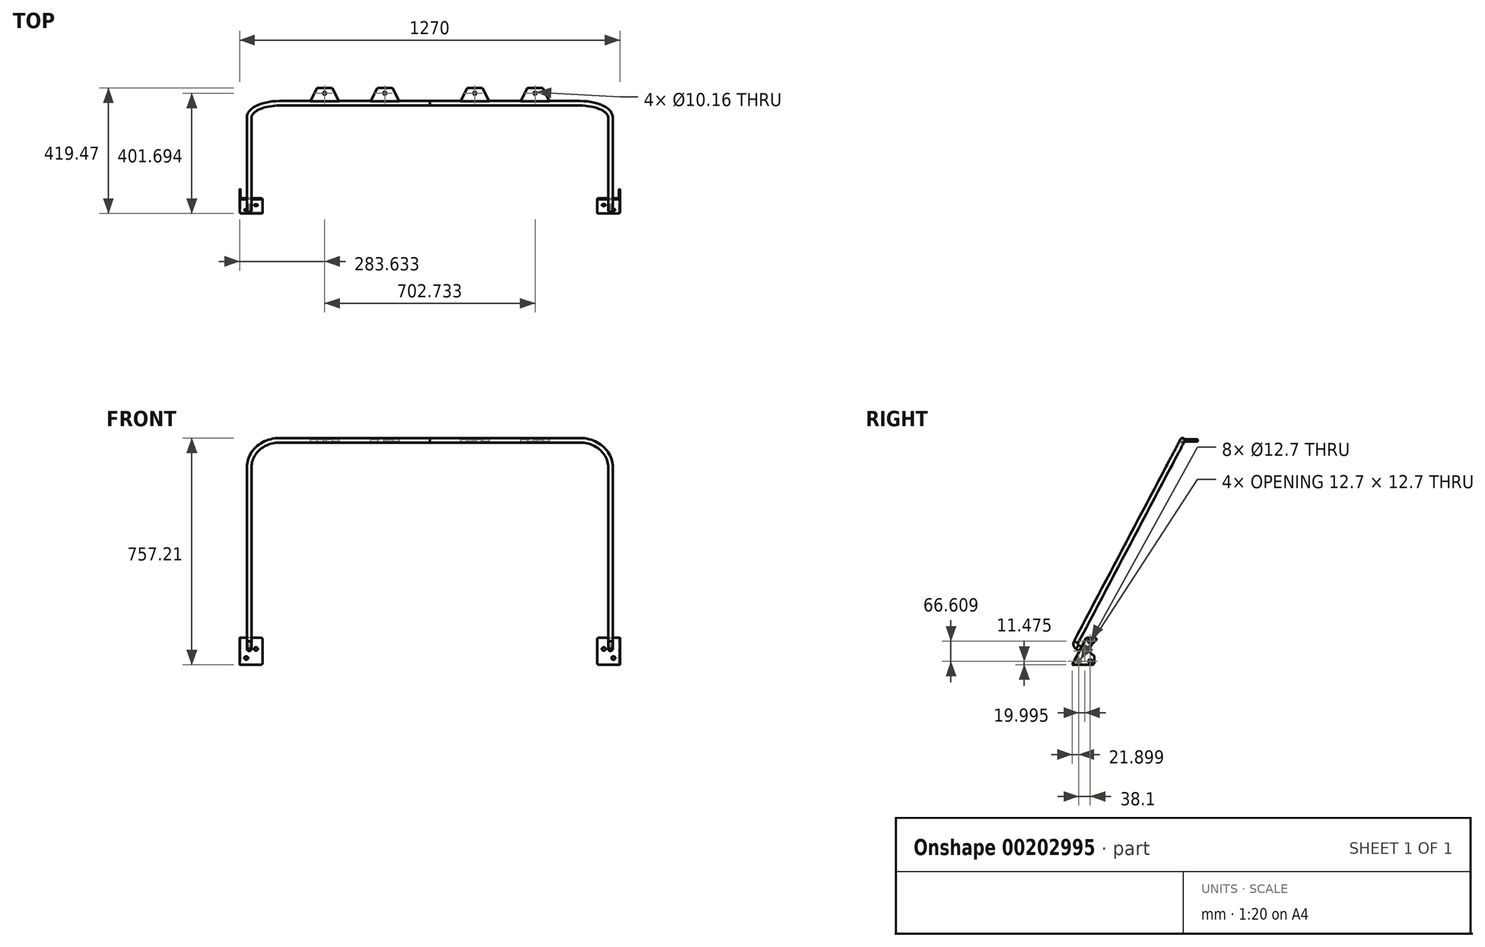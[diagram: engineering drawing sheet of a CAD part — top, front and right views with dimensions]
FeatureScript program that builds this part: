
annotation { "Feature Type Name" : "Feature", "Feature Type Description" : "" }
export const myFeature = defineFeature(function(context is Context, id is Id, definition is map)
    precondition{}
    {
        {
            var Q0;
            Q0=qCreatedBy(makeId("Right.planeOp"),FACE);
            var sketch = newSketch(context, id + "F0", { "sketchPlane" : qUnion([Q0])});
            skLineSegment(sketch, "E0", {"start": v(0, 0) * mm, "end": v(-47.4, -89.86) * mm});
            skLineSegment(sketch, "E1", {"start": v(-47.4, -89.86) * mm, "end": v(-50.58, -89.86) * mm});
            skLineSegment(sketch, "E2", {"start": v(-50.58, -89.86) * mm, "end": v(-3.17, 0) * mm});
            skLineSegment(sketch, "E3", {"start": v(-3.17, 0) * mm, "end": v(0, 0) * mm});
            skSolve(sketch);
        }
        {
            var Q0;
            Q0 = qSketchRegion(id + "F0", true);
            extrude(context, id + "F1", {"entities" : qUnion([Q0]), "depth" : 76.2 * mm});
        }
        {
            var Q0;
            Q0=qCreatedBy(makeId("Right.planeOp"),FACE);
            var sketch = newSketch(context, id + "F2", { "sketchPlane" : qUnion([Q0])});
            skLineSegment(sketch, "E4", {"start": v(-3.18, 0) * mm, "end": v(-50.58, -89.86) * mm});
            skLineSegment(sketch, "E5", {"start": v(-50.58, -89.86) * mm, "end": v(22.53, -89.86) * mm});
            skLineSegment(sketch, "E6", {"start": v(22.53, -89.86) * mm, "end": v(22.53, -58.72) * mm});
            skLineSegment(sketch, "E7", {"start": v(-3.17, 0) * mm, "end": v(40.86, 0) * mm});
            skFitSpline(sketch, "E8", {"points": [v(40.86, 0) * mm, v(22.53, -58.72) * mm], "startDerivative": vector(-122.58, -77.31) * mm, "endDerivative": vector(65.99, -20.96) * mm});
            skSolve(sketch);
        }
        {
            var Q0;
            Q0 = qSketchRegion(id + "F2", true);
            extrude(context, id + "F3", {"entities" : qUnion([Q0]), "operationType" : NewBodyOperationType.ADD, "depth" : 3.17 * mm});
        }
        {
            var Q0;
            Q0=makeQuery(id+"F1.opExtrude","SWEPT_FACE",FACE,{"disambiguationData":[OSD([sQuery(id+"F0.wireOp",EDGE,"E2")])]});
            var sketch = newSketch(context, id + "F4", { "sketchPlane" : qUnion([Q0])});
            skCircle(sketch, "E9", {"center": v(54.23, -43.4) * mm, "radius": 6.35 * mm});
            skCircle(sketch, "E10", {"center": v(21.97, -77.68) * mm, "radius": 6.35 * mm});
            skSolve(sketch);
        }
        {
            var Q0;
            Q0 = qSketchRegion(id + "F4", true);
            var Q1;
            Q1=makeQuery(id+"F1.opExtrude","SWEPT_FACE",FACE,{"disambiguationData":[OSD([sQuery(id+"F0.wireOp",EDGE,"E0")])]});
            extrude(context, id + "F5", {"entities" : qUnion([Q0]), "operationType" : NewBodyOperationType.REMOVE, "endBound" : BoundingType.UP_TO_SURFACE, "oppositeDirection" : true, "endBoundEntityFace" : qUnion([Q1]), "depth" : 25.4 * mm});
        }
        {
            var Q0;
            Q0=makeQuery(id+"F3.boolean.opBoolean","MERGE",FACE,{"derivedFrom":[makeQuery(id+"F1.opExtrude","CAP_FACE",FACE,{"disambiguationData":[OSD([sQuery(id+"F0.wireOp",EDGE,"E0"),sQuery(id+"F0.wireOp",EDGE,"E1"),sQuery(id+"F0.wireOp",EDGE,"E2"),sQuery(id+"F0.wireOp",EDGE,"E3")])],"isStart":true}),makeQuery(id+"F3.opExtrude","CAP_FACE",FACE,{"disambiguationData":[OSD([sQuery(id+"F2.wireOp",EDGE,"E4"),sQuery(id+"F2.wireOp",EDGE,"E5"),sQuery(id+"F2.wireOp",EDGE,"E6"),sQuery(id+"F2.wireOp",EDGE,"E7"),sQuery(id+"F2.wireOp",EDGE,"E8")])],"isStart":true})]});
            var sketch = newSketch(context, id + "F6", { "sketchPlane" : qUnion([Q0])});
            skCircle(sketch, "E11", {"center": v(-8.56, -11.78) * mm, "radius": 6.35 * mm});
            skCircle(sketch, "E12", {"center": v(8.69, -44.87) * mm, "radius": 6.35 * mm});
            skCircle(sketch, "E13", {"center": v(-9.42, -78.39) * mm, "radius": 6.35 * mm});
            skCircle(sketch, "E14", {"center": v(28.68, -78.39) * mm, "radius": 6.35 * mm});
            skSolve(sketch);
        }
        {
            var Q0;
            Q0 = qSketchRegion(id + "F6", true);
            var Q1;
            Q1=makeQuery(id+"F3.opExtrude","CAP_FACE",FACE,{"disambiguationData":[OSD([sQuery(id+"F2.wireOp",EDGE,"E4"),sQuery(id+"F2.wireOp",EDGE,"E5"),sQuery(id+"F2.wireOp",EDGE,"E6"),sQuery(id+"F2.wireOp",EDGE,"E7"),sQuery(id+"F2.wireOp",EDGE,"E8")])],"isStart":false});
            extrude(context, id + "F7", {"entities" : qUnion([Q0]), "operationType" : NewBodyOperationType.REMOVE, "endBound" : BoundingType.UP_TO_SURFACE, "oppositeDirection" : true, "endBoundEntityFace" : qUnion([Q1]), "depth" : 25.4 * mm});
        }
        {
            var Q0;
            Q0=qCreatedBy(makeId("Right.planeOp"),FACE);
            cPlane(context, id + "F8", {"entities" : qUnion([Q0]), "cplaneType" : CPlaneType.OFFSET, "offset" : 635 * mm, "width" : 152.4 * mm, "height" : 152.4 * mm});
        }
        {
            var Q0;
            Q0=qCreatedBy(makeId("Right.planeOp"),FACE);
            cPlane(context, id + "F9", {"entities" : qUnion([Q0]), "cplaneType" : CPlaneType.OFFSET, "offset" : 31.75 * mm, "width" : 152.4 * mm, "height" : 152.4 * mm});
        }
        {
            var Q0;
            Q0=qCreatedBy(id+"F9.planeOp",FACE);
            var sketch = newSketch(context, id + "F10", { "sketchPlane" : qUnion([Q0])});
            skLineSegment(sketch, "E15", {"start": v(-22.79, -37.18) * mm, "end": v(-33.75, -30.77) * mm});
            skArc(sketch, "E16", {"start": v(-33.75, -30.77) * mm, "mid": v(-39.05, -23.33) * mm, "end": v(-37.97, -14.25) * mm});
            skLineSegment(sketch, "E17", {"start": v(-37.97, -14.25) * mm, "end": v(270.14, 569.86) * mm});
            skLineSegment(sketch, "E18", {"start": v(-37.97, -14.25) * mm, "end": v(-16.63, -25.51) * mm});
            skSolve(sketch);
        }
        {
            var Q0;
            Q0=makeQuery(id+"F1.opExtrude","SWEPT_FACE",FACE,{"disambiguationData":[OSD([sQuery(id+"F0.wireOp",EDGE,"E2")])]});
            cPlane(context, id + "F11", {"entities" : qUnion([Q0]), "cplaneType" : CPlaneType.OFFSET, "offset" : 24.13 * mm, "width" : 152.4 * mm, "height" : 152.4 * mm});
        }
        {
            var Q0;
            Q0=qCreatedBy(id+"F11.planeOp",FACE);
            var sketch = newSketch(context, id + "F12", { "sketchPlane" : qUnion([Q0])});
            skLineSegment(sketch, "E19", {"start": v(133.35, 731.68) * mm, "end": v(635, 731.68) * mm});
            skArc(sketch, "E20", {"start": v(133.35, 731.68) * mm, "mid": v(61.5, 701.92) * mm, "end": v(31.75, 630.08) * mm});
            skPoint(sketch, "E21.orphan", {"position": v(31.75, 630.08) * mm});
            skSolve(sketch);
        }
        {
            var Q0;
            Q0=makeQuery(id+"F1.opExtrude","SWEPT_FACE",FACE,{"disambiguationData":[OSD([sQuery(id+"F0.wireOp",EDGE,"E2")])]});
            var sketch = newSketch(context, id + "F13", { "sketchPlane" : qUnion([Q0])});
            skCircle(sketch, "E22", {"center": v(31.75, -43.52) * mm, "radius": 7.62 * mm});
            skSolve(sketch);
        }
        {
            var Q0;
            Q0=makeQuery(id+"F13.imprint","IMPRINT",FACE,{"disambiguationData":[TD([[makeQuery(id+"F13.imprint","IMPRINT",EDGE,{"derivedFrom":sQuery(id+"F13.wireOp",EDGE,"E22")}),1.0]])]});
            var Q1;
            Q1=sQuery(id+"F10.wireOp",EDGE,"E15");
            var Q2;
            Q2=sQuery(id+"F10.wireOp",EDGE,"E16");
            var Q3;
            Q3=sQuery(id+"F10.wireOp",EDGE,"E17");
            var Q4;
            Q4=sQuery(id+"F12.wireOp",EDGE,"E20");
            var Q5;
            Q5=sQuery(id+"F12.wireOp",EDGE,"E19");
            sweep(context, id + "F14", {"operationType" : NewBodyOperationType.ADD, "profiles" : qUnion([Q0]), "path" : qUnion([Q1, Q2, Q3, Q4, Q5])});
        }
        {
            var Q0;
            Q0=makeQuery(id+"F1.opExtrude","CAP_EDGE",EDGE,{"disambiguationData":[OSD([sQuery(id+"F0.wireOp",EDGE,"E3")])],"isStart":false});
            var Q1;
            Q1=makeQuery(id+"F1.opExtrude","CAP_EDGE",EDGE,{"disambiguationData":[OSD([sQuery(id+"F0.wireOp",EDGE,"E1")])],"isStart":false});
            var Q2;
            Q2=makeQuery(id+"F3.opExtrude","SWEPT_EDGE",EDGE,{"disambiguationData":[OSD([sQuery(id+"F2.wireOp",EDGE,"E5"),sQuery(id+"F2.wireOp",EDGE,"E6")])]});
            var Q3;
            Q3=makeQuery(id+"F3.opExtrude","SWEPT_EDGE",EDGE,{"disambiguationData":[OSD([sQuery(id+"F2.wireOp",EDGE,"E6"),sQuery(id+"F2.wireOp",EDGE,"E8")])]});
            var Q4;
            Q4=makeQuery(id+"F3.opExtrude","SWEPT_EDGE",EDGE,{"disambiguationData":[OSD([sQuery(id+"F2.wireOp",EDGE,"E7"),sQuery(id+"F2.wireOp",EDGE,"E8")])]});
            fillet(context, id + "F15", {"entities" : qUnion([Q0, Q1, Q2, Q3, Q4]), "radius" : 5.08 * mm, "tangentPropagation" : true, "allowEdgeOverflow" : false});
        }
        {
            var Q0;
            Q0=makeQuery(id+"F1.opExtrude","CAP_EDGE",EDGE,{"disambiguationData":[OSD([sQuery(id+"F0.wireOp",EDGE,"E2")])],"isStart":true});
            fillet(context, id + "F16", {"entities" : qUnion([Q0]), "radius" : 5.08 * mm, "tangentPropagation" : true, "allowEdgeOverflow" : false});
        }
        {
            var Q0;
            Q0=qCreatedBy(id+"F9.planeOp",FACE);
            cPlane(context, id + "F17", {"entities" : qUnion([Q0]), "cplaneType" : CPlaneType.OFFSET, "offset" : 101.6 * mm, "width" : 152.4 * mm, "height" : 152.4 * mm});
        }
        {
            var Q0;
            Q0=qCreatedBy(id+"F17.planeOp",FACE);
            var sketch = newSketch(context, id + "F18", { "sketchPlane" : qUnion([Q0])});
            skLineSegment(sketch, "E23", {"start": v(0, 0) * mm, "end": v(0, 659.73) * mm});
            skSolve(sketch);
        }
        {
            var Q0;
            Q0=qCreatedBy(makeId("Top.planeOp"),FACE);
            var Q1;
            Q1=sQuery(id+"F18.wireOp",VERTEX,"E23.end");
            cPlane(context, id + "F19", {"entities" : qUnion([Q0, Q1]), "cplaneType" : CPlaneType.PLANE_POINT, "offset" : 25.4 * mm, "width" : 152.4 * mm, "height" : 152.4 * mm});
        }
        {
            var Q0;
            Q0=qCreatedBy(id+"F19.planeOp",FACE);
            var sketch = newSketch(context, id + "F20", { "sketchPlane" : qUnion([Q0])});
            skLineSegment(sketch, "E24", {"start": v(232.83, 317.54) * mm, "end": v(258.23, 368.9) * mm});
            skLineSegment(sketch, "E25", {"start": v(283.63, 317.54) * mm, "end": v(283.63, 484.17) * mm});
            skLineSegment(sketch, "E26", {"start": v(258.23, 368.9) * mm, "end": v(283.63, 368.9) * mm});
            skPoint(sketch, "E26.endSnap0", {"position": v(283.63, 400.86) * mm});
            skLineSegment(sketch, "E27", {"start": v(232.83, 317.54) * mm, "end": v(283.63, 317.54) * mm});
            skLineSegment(sketch, "E28.MirrorCS", {"start": v(309.03, 368.9) * mm, "end": v(283.63, 368.9) * mm});
            skLineSegment(sketch, "E29.MirrorCS", {"start": v(334.43, 317.54) * mm, "end": v(309.03, 368.9) * mm});
            skLineSegment(sketch, "E30.MirrorCS", {"start": v(334.43, 317.54) * mm, "end": v(283.63, 317.54) * mm});
            skCircle(sketch, "E31", {"center": v(283.63, 351.11) * mm, "radius": 5.08 * mm});
            skLineSegment(sketch, "E32", {"start": v(384.18, 317.54) * mm, "end": v(384.18, 479.63) * mm});
            skLineSegment(sketch, "E33.MirrorCS", {"start": v(433.92, 317.54) * mm, "end": v(459.32, 368.9) * mm});
            skLineSegment(sketch, "E34.MirrorCS", {"start": v(459.32, 368.9) * mm, "end": v(484.72, 368.9) * mm});
            skLineSegment(sketch, "E35.MirrorCS", {"start": v(510.12, 368.9) * mm, "end": v(484.72, 368.9) * mm});
            skLineSegment(sketch, "E36.MirrorCS", {"start": v(535.52, 317.54) * mm, "end": v(510.12, 368.9) * mm});
            skLineSegment(sketch, "E37.MirrorCS", {"start": v(535.52, 317.54) * mm, "end": v(484.72, 317.54) * mm});
            skLineSegment(sketch, "E38.MirrorCS", {"start": v(433.92, 317.54) * mm, "end": v(484.72, 317.54) * mm});
            skCircle(sketch, "E39.MirrorC", {"center": v(484.72, 351.11) * mm, "radius": 5.08 * mm});
            skSolve(sketch);
        }
        {
            var Q0;
            Q0 = qSketchRegion(id + "F20", true);
            extrude(context, id + "F21", {"entities" : qUnion([Q0]), "depth" : 3.8 * mm, "hasSecondDirection" : true, "secondDirectionOppositeDirection" : true, "secondDirectionDepth" : 3.8 * mm});
        }
        {
            var Q0;
            Q0=makeQuery(id+"F1.opExtrude","SWEPT_BODY",BODY,{"disambiguationData":[OSD([sQuery(id+"F0.wireOp",EDGE,"E0"),sQuery(id+"F0.wireOp",EDGE,"E1"),sQuery(id+"F0.wireOp",EDGE,"E2"),sQuery(id+"F0.wireOp",EDGE,"E3")])]});
            var Q1;
            Q1=makeQuery(id+"F21.opExtrude","SWEPT_BODY",BODY,{"disambiguationData":[OSD([sQuery(id+"F20.wireOp",EDGE,"E24"),sQuery(id+"F20.wireOp",EDGE,"E26"),sQuery(id+"F20.wireOp",EDGE,"E27"),sQuery(id+"F20.wireOp",EDGE,"E28.MirrorCS"),sQuery(id+"F20.wireOp",EDGE,"E29.MirrorCS"),sQuery(id+"F20.wireOp",EDGE,"E30.MirrorCS"),sQuery(id+"F20.wireOp",EDGE,"E31")])]});
            var Q2;
            Q2=makeQuery(id+"F21.opExtrude","SWEPT_BODY",BODY,{"disambiguationData":[OSD([sQuery(id+"F20.wireOp",EDGE,"E33.MirrorCS"),sQuery(id+"F20.wireOp",EDGE,"E34.MirrorCS"),sQuery(id+"F20.wireOp",EDGE,"E35.MirrorCS"),sQuery(id+"F20.wireOp",EDGE,"E36.MirrorCS"),sQuery(id+"F20.wireOp",EDGE,"E37.MirrorCS"),sQuery(id+"F20.wireOp",EDGE,"E38.MirrorCS"),sQuery(id+"F20.wireOp",EDGE,"E39.MirrorC")])]});
            var Q3;
            Q3=qCreatedBy(id+"F8.planeOp",FACE);
            mirror(context, id + "F22", {"operationType" : NewBodyOperationType.ADD, "entities" : qUnion([Q0, Q1, Q2]), "mirrorPlane" : qUnion([Q3])});
        }
    });
